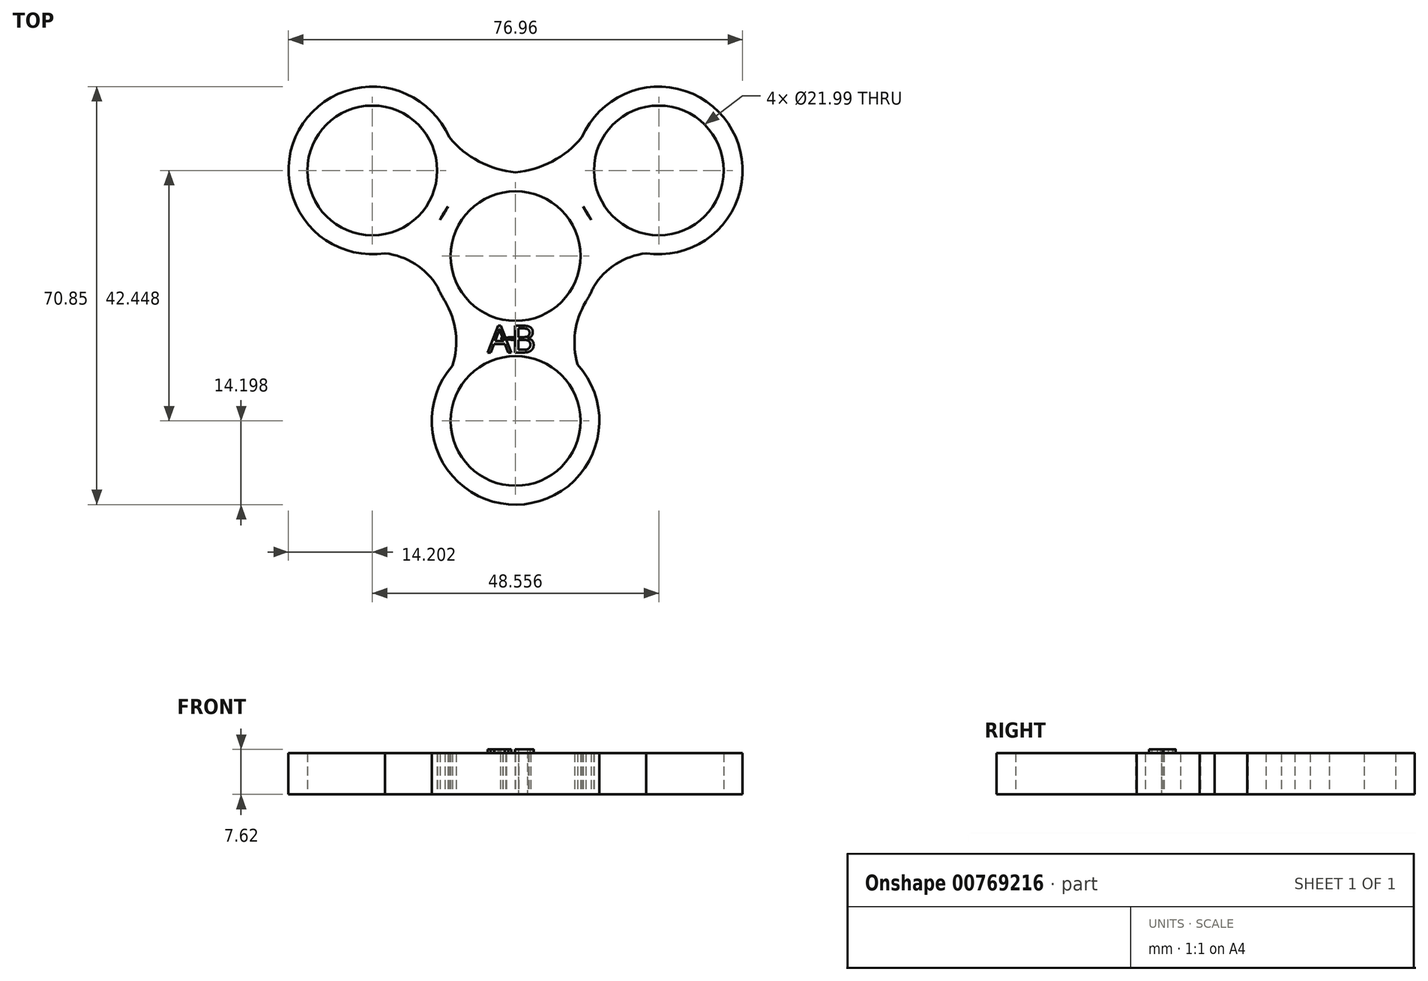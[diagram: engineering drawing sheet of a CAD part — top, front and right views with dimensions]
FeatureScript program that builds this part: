
annotation { "Feature Type Name" : "Feature", "Feature Type Description" : "" }
export const myFeature = defineFeature(function(context is Context, id is Id, definition is map)
    precondition{}
    {
        {
            var Q0;
            Q0=qCreatedBy(makeId("Top.planeOp"),FACE);
            var sketch = newSketch(context, id + "F0", { "sketchPlane" : qUnion([Q0])});
            skCircle(sketch, "E0", {"center": v(0, 0) * mm, "radius": 11 * mm});
            skCircle(sketch, "E1", {"center": v(-24.28, 14.5) * mm, "radius": 11 * mm});
            skCircle(sketch, "E2", {"center": v(0, -27.94) * mm, "radius": 11 * mm});
            skCircle(sketch, "E3", {"center": v(0, 0) * mm, "radius": 14.2 * mm});
            skCircle(sketch, "E4", {"center": v(0, -27.94) * mm, "radius": 14.2 * mm});
            skCircle(sketch, "E5", {"center": v(-24.28, 14.5) * mm, "radius": 14.2 * mm});
            skCircle(sketch, "E6.MirrorC", {"center": v(24.28, 14.5) * mm, "radius": 14.2 * mm});
            skCircle(sketch, "E7.MirrorC", {"center": v(24.28, 14.5) * mm, "radius": 11 * mm});
            skArc(sketch, "E8", {"start": v(0, 14.2) * mm, "mid": v(8.05, 17.17) * mm, "end": v(13.53, 23.78) * mm});
            skArc(sketch, "E9.MirrorCS", {"start": v(0, 14.2) * mm, "mid": v(-8.05, 17.17) * mm, "end": v(-13.53, 23.78) * mm});
            skArc(sketch, "E10", {"start": v(-12.15, -7.35) * mm, "mid": v(-16.03, -2.04) * mm, "end": v(-22.1, 0.47) * mm});
            skArc(sketch, "E11.MirrorCS", {"start": v(12.15, -7.35) * mm, "mid": v(16.03, -2.04) * mm, "end": v(22.1, 0.47) * mm});
            skArc(sketch, "E12", {"start": v(-13.46, -23.4) * mm, "mid": v(-10.1, -15.6) * mm, "end": v(-12.15, -7.35) * mm});
            skArc(sketch, "E13", {"start": v(12.15, -7.35) * mm, "mid": v(10.03, -15.82) * mm, "end": v(13.59, -23.8) * mm});
            skSolve(sketch);
        }
        {
            var Q0;
            Q0 = qSketchRegion(id + "F0", true);
            extrude(context, id + "F1", {"entities" : qUnion([Q0]), "depth" : 7 * mm, "offsetDistance" : 25.4 * mm});
        }
        {
            var Q0;
            Q0=qCreatedBy(makeId("Top.planeOp"),FACE);
            var sketch = newSketch(context, id + "F2", { "sketchPlane" : qUnion([Q0])});
            skText(sketch, "E14", { "text": "AB", "fontName": "OpenSans-Regular.ttf"});
            const initialGuessF2  = {"E14": [-0.00473, -0.01634, 1, 0, 0.00458]};
            skSetInitialGuess(sketch, initialGuessF2);
            skSolve(sketch);
        }
        {
            var Q0;
            Q0 = qSketchRegion(id + "F2", true);
            extrude(context, id + "F3", {"entities" : qUnion([Q0]), "operationType" : NewBodyOperationType.ADD, "depth" : 7.62 * mm, "offsetDistance" : 25.4 * mm});
        }
    });
